# Revit family: BC_Hitachi_KPI-EX-4E-502-1002_LOD400
name_source: partatom
category: Equipement de génie climatique
revit_build: Autodesk Revit 2016 (Build: 20150220_1215(x64)
units: mm (PartAtom-declared; Revit-internal decimal feet)

## family parameters
Basée sur le plan de construction = Non
Cote de connecteur circulaire = Utiliser le diamètre
Couper avec des vides une fois chargée = Non
Numéro OmniClass = 23.75.50.00
Partagée = Non
Point de calcul de pièce = Non
Titre OmniClass = Energy Treatment
Toujours verticalement = Oui
Type d'élément = Normal

## types (3) — shared parameters
Color = Neutral white (4.56Y8.85/0.38)
Description = Ventilation unit with heat recovery. Optional CO2 sensor control
Fabricant = HITACHI
Frequency = 50 Hz
Mass = 0.00 kg
Maximum AC Voltage = 253 V
Minimum AC Voltage = 207 V
Modèle = Heat recovery KPI
Nominal Voltage = 230 V
Number of Poles = 1
Outlet Diameter = 32.00 mm
Refrigerant = R410A (factory-charged corrosion-proof nitrogen)
Usage Current = 4 A

## per-type parameters (varying)
- KPI-1002X4E: Air flow rate (Hi/Me/low) m3/h=1000/820/740; Air in to room depth=68.00 mm; Air out of room depth=64.00 mm; Commentaires du type=KPI-1002X4E; Cooling Capacity=11 kW; Electrical box depth=101.00 mm; Enthalpy exchange for cooling (%)=62; Enthalpy exchange for heating (%)=68; Exhaust air diameter=300.00 mm; Gas Diameter=15.88 mm; Heating Capacity=13 kW; Liquid Diameter=9.52 mm; Maximum Air Flow=1000.0 m³/h; Maximum external pressure  (nom. air flow)=170.0 Pa; Minimum Air Flow=740.0 m³/h; Nominal power input (Hi/me/low) W=357/198/150; Output Diameter=300.00 mm; Overall Depth=385.00 mm; Overall Height=1904.00 mm; Overall Width=1295.00 mm; Product Code=70603203; Return air diameter=300.00 mm; Sound power at medium load (dB(A))=33; Sound power at minimal load (dB(A))=31; Sound power level (High) dB(A)=54; Sound power max (dB(A))=36; Static pressure=170/105/80; Supply Air Diameter=300.00 mm; Temperature exchange efficiency (High/me/low) %=76/78/79
- KPI 802 X 4E: Air flow rate (Hi/Me/low) m3/h=800/700/590; Air in to room depth=90.00 mm; Air out of room depth=85.00 mm; Commentaires du type=KPI-802X4E; Cooling Capacity=8 kW; Electrical box depth=121.00 mm; Enthalpy exchange for cooling (%)=62; Enthalpy exchange for heating (%)=65; Exhaust air diameter=250.00 mm; Gas Diameter=15.88 mm; Heating Capacity=10 kW; Liquid Diameter=6.35 mm; Maximum Air Flow=800.0 m³/h; Maximum external pressure  (nom. air flow)=110.0 Pa; Minimum Air Flow=590.0 m³/h; Nominal power input (Hi/me/low) W=255/161/108; Output Diameter=250.00 mm; Overall Depth=385.00 mm; Overall Height=1513.00 mm; Overall Width=1015.00 mm; Product Code=70603202; Return air diameter=250.00 mm; Sound power at medium load (dB(A))=33; Sound power at minimal load (dB(A))=32; Sound power level (High) dB(A)=53; Sound power max (dB(A))=34; Static pressure=110/80/57; Supply Air Diameter=250.00 mm; Temperature exchange efficiency (High/me/low) %=76/78/79
- KPI-502X4E: Air flow rate (Hi/Me/low) m3/h=500/430/380; Air in to room depth=90.00 mm; Air out of room depth=85.00 mm; Commentaires du type=KPI-502X4E; Cooling Capacity=5 kW; Electrical box depth=121.00 mm; Enthalpy exchange for cooling (%)=61; Enthalpy exchange for heating (%)=65; Exhaust air diameter=200.00 mm; Gas Diameter=12.70 mm; Heating Capacity=7 kW; Liquid Diameter=6.35 mm; Maximum Air Flow=500.0 m³/h; Maximum external pressure  (nom. air flow)=165.0 Pa; Minimum Air Flow=380.0 m³/h; Nominal power input (Hi/me/low) W=130/95/73; Output Diameter=200.00 mm; Overall Depth=330.00 mm; Overall Height=1435.00 mm; Overall Width=920.00 mm; Product Code=70603201; Return air diameter=200.00 mm; Sound power at medium load (dB(A))=30; Sound power at minimal load (dB(A))=29; Sound power level (High) dB(A)=50; Sound power max (dB(A))=32; Static pressure=90/82/60; Supply Air Diameter=200.00 mm; Temperature exchange efficiency (High/me/low) %=73/75/76

## geometry (parser evidence)
native form markers: Blend x2
no freeform markers — native parametric forms only
